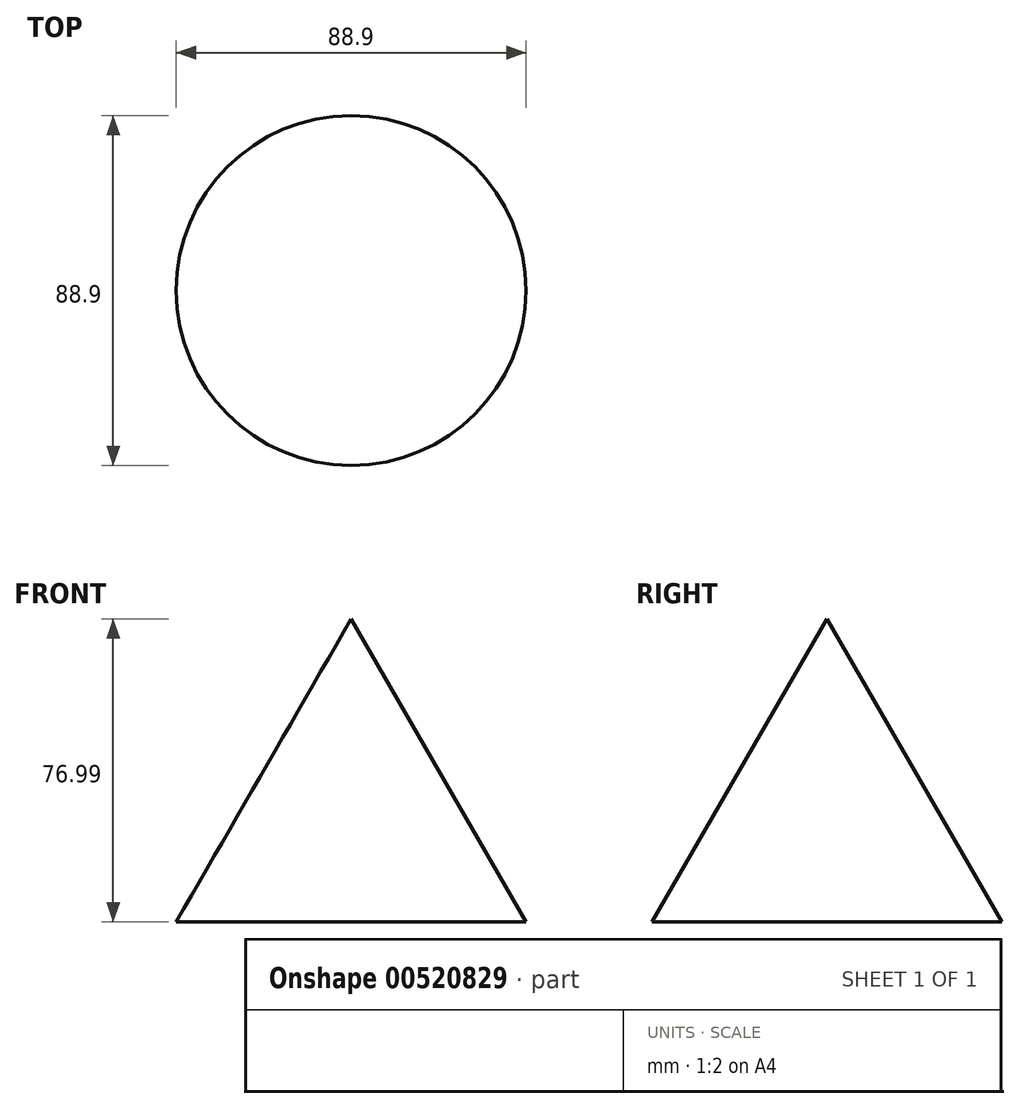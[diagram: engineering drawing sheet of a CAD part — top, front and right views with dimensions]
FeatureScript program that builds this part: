
annotation { "Feature Type Name" : "Feature", "Feature Type Description" : "" }
export const myFeature = defineFeature(function(context is Context, id is Id, definition is map)
    precondition{}
    {
        {
            var Q0;
            Q0=qCreatedBy(makeId("Front.planeOp"),FACE);
            var sketch = newSketch(context, id + "F0", { "sketchPlane" : qUnion([Q0])});
            skLineSegment(sketch, "E0", {"start": v(-44.45, 0) * mm, "end": v(0, 76.99) * mm});
            skLineSegment(sketch, "E1", {"start": v(-44.45, 0) * mm, "end": v(0, 0) * mm});
            skLineSegment(sketch, "E2", {"start": v(0, 76.99) * mm, "end": v(0, 0) * mm});
            skSolve(sketch);
        }
        {
            var Q0;
            Q0=makeQuery(id+"F0.imprint","IMPRINT",FACE,{"disambiguationData":[TD([[makeQuery(id+"F0.imprint","IMPRINT",EDGE,{"derivedFrom":sQuery(id+"F0.wireOp",EDGE,"E0")}),-1.0]])]});
            var Q1;
            Q1=sQuery(id+"F0.wireOp",EDGE,"E2");
            revolve(context, id + "F1", {"entities" : qUnion([Q0]), "axis" : qUnion([Q1]), "revolveType" : RevolveType.FULL});
        }
    });
